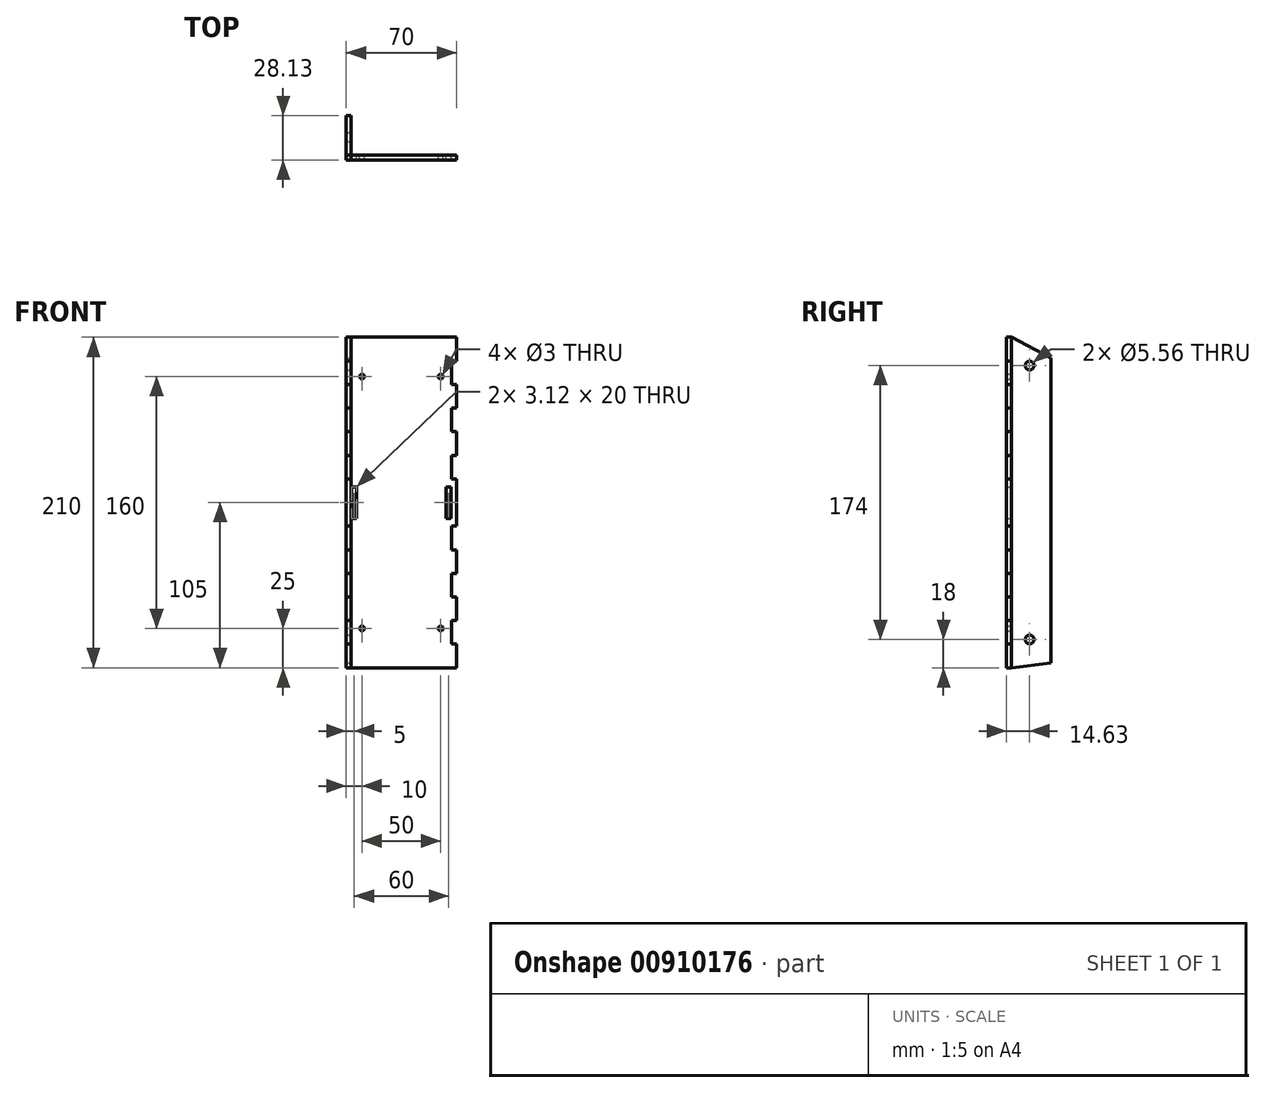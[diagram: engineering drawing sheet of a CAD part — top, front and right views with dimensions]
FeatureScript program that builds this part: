
annotation { "Feature Type Name" : "Feature", "Feature Type Description" : "" }
export const myFeature = defineFeature(function(context is Context, id is Id, definition is map)
    precondition{}
    {
        {
            assignVariable(context, id + "F0", {"name" : "Width", "anyValue" : 3.12});
        }
        {
            var Q0;
            Q0=qCreatedBy(makeId("Front.planeOp"),FACE);
            var sketch = newSketch(context, id + "F1", { "sketchPlane" : qUnion([Q0])});
            skLineSegment(sketch, "E0", {"start": v(0, 0) * mm, "end": v(25, 0) * mm, "construction": true});
            skCircle(sketch, "E1", {"center": v(25, 0) * mm, "radius": 1.5 * mm});
            skLineSegment(sketch, "E2", {"start": v(0, -25) * mm, "end": v(35, -25) * mm});
            skLineSegment(sketch, "E3", {"start": v(35, -25) * mm, "end": v(35, -10) * mm});
            skLineSegment(sketch, "E4", {"start": v(35, -10) * mm, "end": v(31.88, -10) * mm});
            skLineSegment(sketch, "E5", {"start": v(31.88, -10) * mm, "end": v(31.88, 5) * mm});
            skLineSegment(sketch, "E6", {"start": v(31.88, 5) * mm, "end": v(35, 5) * mm});
            skLineSegment(sketch, "E7.1.0.0", {"start": v(31.88, 35) * mm, "end": v(35, 35) * mm});
            skLineSegment(sketch, "E7.1.0.1", {"start": v(31.88, 20) * mm, "end": v(31.88, 35) * mm});
            skLineSegment(sketch, "E7.1.0.2", {"start": v(35, 20) * mm, "end": v(31.88, 20) * mm});
            skLineSegment(sketch, "E7.1.0.3", {"start": v(35, 5) * mm, "end": v(35, 20) * mm});
            skLineSegment(sketch, "E7.2.0.0", {"start": v(31.88, 65) * mm, "end": v(35, 65) * mm});
            skLineSegment(sketch, "E7.2.0.1", {"start": v(31.88, 50) * mm, "end": v(31.88, 65) * mm});
            skLineSegment(sketch, "E7.2.0.2", {"start": v(35, 50) * mm, "end": v(31.88, 50) * mm});
            skLineSegment(sketch, "E7.2.0.3", {"start": v(35, 35) * mm, "end": v(35, 50) * mm});
            skLineSegment(sketch, "E7.direction1", {"start": v(31.88, 5) * mm, "end": v(31.88, 35) * mm, "construction": true});
            skLineSegment(sketch, "E8", {"start": v(35, 65) * mm, "end": v(35, 80) * mm});
            skLineSegment(sketch, "E9", {"start": v(35, 80) * mm, "end": v(0, 80) * mm, "construction": true});
            skLineSegment(sketch, "E10", {"start": v(0, 80) * mm, "end": v(0, 0) * mm, "construction": true});
            skLineSegment(sketch, "E11.MirrorCS", {"start": v(31.88, 155) * mm, "end": v(35, 155) * mm});
            skLineSegment(sketch, "E12.MirrorCS", {"start": v(31.88, 125) * mm, "end": v(35, 125) * mm});
            skLineSegment(sketch, "E13.MirrorCS", {"start": v(31.88, 95) * mm, "end": v(35, 95) * mm});
            skCircle(sketch, "E14.MirrorC", {"center": v(25, 160) * mm, "radius": 1.5 * mm});
            skLineSegment(sketch, "E15.MirrorCS", {"start": v(35, 140) * mm, "end": v(31.88, 140) * mm});
            skLineSegment(sketch, "E16.MirrorCS", {"start": v(35, 170) * mm, "end": v(31.88, 170) * mm});
            skLineSegment(sketch, "E17.MirrorCS", {"start": v(35, 110) * mm, "end": v(31.88, 110) * mm});
            skLineSegment(sketch, "E18.MirrorCS", {"start": v(31.88, 140) * mm, "end": v(31.88, 125) * mm});
            skLineSegment(sketch, "E19.MirrorCS", {"start": v(31.88, 170) * mm, "end": v(31.88, 155) * mm});
            skLineSegment(sketch, "E20.MirrorCS", {"start": v(31.88, 110) * mm, "end": v(31.88, 95) * mm});
            skLineSegment(sketch, "E21.MirrorCS", {"start": v(31.88, 155) * mm, "end": v(31.88, 125) * mm, "construction": true});
            skLineSegment(sketch, "E22.MirrorCS", {"start": v(0, 160) * mm, "end": v(25, 160) * mm, "construction": true});
            skLineSegment(sketch, "E23.MirrorCS", {"start": v(0, 80) * mm, "end": v(0, 160) * mm, "construction": true});
            skLineSegment(sketch, "E24.MirrorCS", {"start": v(35, 125) * mm, "end": v(35, 110) * mm});
            skLineSegment(sketch, "E25.MirrorCS", {"start": v(35, 155) * mm, "end": v(35, 140) * mm});
            skLineSegment(sketch, "E26.MirrorCS", {"start": v(35, 95) * mm, "end": v(35, 80) * mm});
            skLineSegment(sketch, "E27.MirrorCS", {"start": v(0, 185) * mm, "end": v(35, 185) * mm});
            skLineSegment(sketch, "E28.MirrorCS", {"start": v(35, 185) * mm, "end": v(35, 170) * mm});
            skCircle(sketch, "E29.MirrorC", {"center": v(-25, 0) * mm, "radius": 1.5 * mm});
            skLineSegment(sketch, "E30.MirrorCS", {"start": v(-31.88, 35) * mm, "end": v(-35, 35) * mm});
            skLineSegment(sketch, "E31.MirrorCS", {"start": v(-31.88, 5) * mm, "end": v(-35, 5) * mm});
            skLineSegment(sketch, "E32.MirrorCS", {"start": v(-31.88, 20) * mm, "end": v(-31.88, 35) * mm});
            skCircle(sketch, "E33.MirrorC", {"center": v(-25, 160) * mm, "radius": 1.5 * mm});
            skLineSegment(sketch, "E34.MirrorCS", {"start": v(-31.88, 170) * mm, "end": v(-31.88, 155) * mm});
            skLineSegment(sketch, "E35.MirrorCS", {"start": v(-31.88, 125) * mm, "end": v(-35, 125) * mm});
            skLineSegment(sketch, "E36.MirrorCS", {"start": v(-35, 20) * mm, "end": v(-31.88, 20) * mm});
            skLineSegment(sketch, "E37.MirrorCS", {"start": v(-31.88, 155) * mm, "end": v(-35, 155) * mm});
            skLineSegment(sketch, "E38.MirrorCS", {"start": v(-31.88, -10) * mm, "end": v(-31.88, 5) * mm});
            skLineSegment(sketch, "E39.MirrorCS", {"start": v(-35, 110) * mm, "end": v(-31.88, 110) * mm});
            skLineSegment(sketch, "E40.MirrorCS", {"start": v(-35, 5) * mm, "end": v(-35, 20) * mm});
            skLineSegment(sketch, "E41.MirrorCS", {"start": v(-35, 35) * mm, "end": v(-35, 50) * mm});
            skLineSegment(sketch, "E42.MirrorCS", {"start": v(-35, 140) * mm, "end": v(-31.88, 140) * mm});
            skLineSegment(sketch, "E43.MirrorCS", {"start": v(-35, -10) * mm, "end": v(-31.88, -10) * mm});
            skLineSegment(sketch, "E44.MirrorCS", {"start": v(-31.88, 65) * mm, "end": v(-35, 65) * mm});
            skLineSegment(sketch, "E45.MirrorCS", {"start": v(-31.88, 140) * mm, "end": v(-31.88, 125) * mm});
            skLineSegment(sketch, "E46.MirrorCS", {"start": v(-31.88, 5) * mm, "end": v(-31.88, 35) * mm, "construction": true});
            skLineSegment(sketch, "E47.MirrorCS", {"start": v(-31.88, 95) * mm, "end": v(-35, 95) * mm});
            skLineSegment(sketch, "E48.MirrorCS", {"start": v(-31.88, 50) * mm, "end": v(-31.88, 65) * mm});
            skLineSegment(sketch, "E49.MirrorCS", {"start": v(-35, 50) * mm, "end": v(-31.88, 50) * mm});
            skLineSegment(sketch, "E50.MirrorCS", {"start": v(-35, 95) * mm, "end": v(-35, 80) * mm});
            skLineSegment(sketch, "E51.MirrorCS", {"start": v(-35, 170) * mm, "end": v(-31.88, 170) * mm});
            skLineSegment(sketch, "E52.MirrorCS", {"start": v(-35, 125) * mm, "end": v(-35, 110) * mm});
            skLineSegment(sketch, "E53.MirrorCS", {"start": v(-31.88, 110) * mm, "end": v(-31.88, 95) * mm});
            skLineSegment(sketch, "E54.MirrorCS", {"start": v(-35, 185) * mm, "end": v(-35, 170) * mm});
            skLineSegment(sketch, "E55.MirrorCS", {"start": v(-35, 155) * mm, "end": v(-35, 140) * mm});
            skLineSegment(sketch, "E56.MirrorCS", {"start": v(-35, 65) * mm, "end": v(-35, 80) * mm});
            skLineSegment(sketch, "E57.MirrorCS", {"start": v(-35, -25) * mm, "end": v(-35, -10) * mm});
            skLineSegment(sketch, "E58.MirrorCS", {"start": v(-31.88, 155) * mm, "end": v(-31.88, 125) * mm, "construction": true});
            skLineSegment(sketch, "E59.MirrorCS", {"start": v(0, -25) * mm, "end": v(-35, -25) * mm});
            skLineSegment(sketch, "E60.MirrorCS", {"start": v(0, 0) * mm, "end": v(-25, 0) * mm, "construction": true});
            skLineSegment(sketch, "E61.MirrorCS", {"start": v(0, 185) * mm, "end": v(-35, 185) * mm});
            skLineSegment(sketch, "E62.MirrorCS", {"start": v(0, 160) * mm, "end": v(-25, 160) * mm, "construction": true});
            skLineSegment(sketch, "E63.MirrorCS", {"start": v(-35, 80) * mm, "end": v(0, 80) * mm, "construction": true});
            skLineSegment(sketch, "E64.bottom", {"start": v(31.56, 70) * mm, "end": v(28.44, 70) * mm});
            skLineSegment(sketch, "E64.top", {"start": v(31.56, 90) * mm, "end": v(28.44, 90) * mm});
            skLineSegment(sketch, "E64.left", {"start": v(31.56, 70) * mm, "end": v(31.56, 90) * mm});
            skLineSegment(sketch, "E64.right", {"start": v(28.44, 70) * mm, "end": v(28.44, 90) * mm});
            skPoint(sketch, "E64.middle", {"position": v(30, 80) * mm});
            skPoint(sketch, "E65.MirrorP", {"position": v(-30, 80) * mm});
            skLineSegment(sketch, "E66.MirrorCS", {"start": v(-31.56, 90) * mm, "end": v(-28.44, 90) * mm});
            skLineSegment(sketch, "E67.MirrorCS", {"start": v(-31.56, 70) * mm, "end": v(-28.44, 70) * mm});
            skLineSegment(sketch, "E68.MirrorCS", {"start": v(-28.44, 70) * mm, "end": v(-28.44, 90) * mm});
            skLineSegment(sketch, "E69.MirrorCS", {"start": v(-31.56, 70) * mm, "end": v(-31.56, 90) * mm});
            skSolve(sketch);
        }
        {
            var Q0;
            Q0 = qSketchRegion(id + "F1", true);
            extrude(context, id + "F2", {"entities" : qUnion([Q0]), "depth" : (getVariable(context, 'Width')) * mm, "offsetDistance" : 25 * mm});
        }
        {
            var Q0;
            Q0=makeQuery(id+"F2.opExtrude","SWEPT_FACE",FACE,{"disambiguationData":[OSD([sQuery(id+"F1.wireOp",EDGE,"E53.MirrorCS")])]});
            var sketch = newSketch(context, id + "F3", { "sketchPlane" : qUnion([Q0])});
            skLineSegment(sketch, "E70", {"start": v(0, -25) * mm, "end": v(3.12, -25) * mm});
            skLineSegment(sketch, "E71", {"start": v(3.12, -25) * mm, "end": v(3.12, -10) * mm});
            skLineSegment(sketch, "E72", {"start": v(3.12, -10) * mm, "end": v(0, -10) * mm});
            skLineSegment(sketch, "E73", {"start": v(0, -10) * mm, "end": v(0, 5) * mm});
            skLineSegment(sketch, "E74", {"start": v(0, 5) * mm, "end": v(3.12, 5) * mm});
            skLineSegment(sketch, "E75.1.0.0", {"start": v(3.12, 5) * mm, "end": v(3.12, 20) * mm});
            skLineSegment(sketch, "E75.1.0.1", {"start": v(0, 20) * mm, "end": v(0, 35) * mm});
            skLineSegment(sketch, "E75.1.0.2", {"start": v(3.12, 20) * mm, "end": v(0, 20) * mm});
            skLineSegment(sketch, "E75.1.0.3", {"start": v(0, 35) * mm, "end": v(3.12, 35) * mm});
            skLineSegment(sketch, "E75.2.0.0", {"start": v(3.12, 35) * mm, "end": v(3.12, 50) * mm});
            skLineSegment(sketch, "E75.2.0.1", {"start": v(0, 50) * mm, "end": v(0, 65) * mm});
            skLineSegment(sketch, "E75.2.0.2", {"start": v(3.12, 50) * mm, "end": v(0, 50) * mm});
            skLineSegment(sketch, "E75.2.0.3", {"start": v(0, 65) * mm, "end": v(3.12, 65) * mm});
            skLineSegment(sketch, "E75.direction1", {"start": v(3.12, -25) * mm, "end": v(3.12, 5) * mm, "construction": true});
            skLineSegment(sketch, "E76", {"start": v(0, 80) * mm, "end": v(3.12, 80) * mm, "construction": true});
            skLineSegment(sketch, "E77.MirrorCS", {"start": v(0, 155) * mm, "end": v(3.12, 155) * mm});
            skLineSegment(sketch, "E78.MirrorCS", {"start": v(0, 185) * mm, "end": v(3.12, 185) * mm});
            skLineSegment(sketch, "E79.MirrorCS", {"start": v(3.12, 170) * mm, "end": v(0, 170) * mm});
            skLineSegment(sketch, "E80.MirrorCS", {"start": v(3.12, 140) * mm, "end": v(0, 140) * mm});
            skLineSegment(sketch, "E81.MirrorCS", {"start": v(3.12, 110) * mm, "end": v(0, 110) * mm});
            skLineSegment(sketch, "E82.MirrorCS", {"start": v(0, 125) * mm, "end": v(3.12, 125) * mm});
            skLineSegment(sketch, "E83.MirrorCS", {"start": v(0, 95) * mm, "end": v(3.12, 95) * mm});
            skLineSegment(sketch, "E84.MirrorCS", {"start": v(3.12, 185) * mm, "end": v(3.12, 170) * mm});
            skLineSegment(sketch, "E85.MirrorCS", {"start": v(3.12, 185) * mm, "end": v(3.12, 155) * mm, "construction": true});
            skLineSegment(sketch, "E86.MirrorCS", {"start": v(3.12, 155) * mm, "end": v(3.12, 140) * mm});
            skLineSegment(sketch, "E87.MirrorCS", {"start": v(0, 110) * mm, "end": v(0, 95) * mm});
            skLineSegment(sketch, "E88.MirrorCS", {"start": v(3.12, 125) * mm, "end": v(3.12, 110) * mm});
            skLineSegment(sketch, "E89.MirrorCS", {"start": v(0, 170) * mm, "end": v(0, 155) * mm});
            skLineSegment(sketch, "E90.MirrorCS", {"start": v(0, 140) * mm, "end": v(0, 125) * mm});
            skLineSegment(sketch, "E91", {"start": v(3.12, 95) * mm, "end": v(3.12, 65) * mm});
            skLineSegment(sketch, "E92", {"start": v(0, 185) * mm, "end": v(-25, 171.8) * mm});
            skLineSegment(sketch, "E93", {"start": v(-25, 171.8) * mm, "end": v(-25, -21.88) * mm});
            skLineSegment(sketch, "E94", {"start": v(-25, -21.88) * mm, "end": v(0, -25) * mm});
            skCircle(sketch, "E95", {"center": v(-11.5, -7) * mm, "radius": 2.78 * mm});
            skCircle(sketch, "E96.MirrorC", {"center": v(-11.5, 167) * mm, "radius": 2.78 * mm});
            skSolve(sketch);
        }
        {
            var Q0;
            Q0=makeQuery(id+"F3.imprint","IMPRINT",FACE,{"disambiguationData":[TD([[makeQuery(id+"F3.imprint","IMPRINT",EDGE,{"derivedFrom":sQuery(id+"F3.wireOp",EDGE,"E74")}),1.0]])]});
            extrude(context, id + "F4", {"entities" : qUnion([Q0]), "depth" : (getVariable(context, 'Width')) * mm, "offsetDistance" : 25 * mm});
        }
    });
